# Revit family: ASL Door Suite 100mm
name_source: partatom
category: Doors
revit_build: Autodesk Revit 2018 (Build: 20170223_1515(x64)
units: mm (PartAtom-declared; Revit-internal decimal feet)

## family parameters
Always vertical = Yes
Cut with Voids When Loaded = No
OmniClass Number = 23.25.20.14.11.11.17
OmniClass Title = Infill Panels
Room Calculation Point = No
Shared = No

## types (5) — shared parameters
Analytic Construction = <None>
Frame Thickness = 44 mm  [stored 0.144357 ft]
Frame Width = 100 mm  [stored 0.328084 ft]
Glass Material = <By Category>
Manufacturer = Aluminate Solutions Limited
Material = <By Category>
Model = ASL Door Suite 100mm
Type Comments = ASL Door Suite 100mm

## per-type parameters (varying)
| type | Head Depth | Kickplate High | URL |
| 100mm Frame | 100 mm  [stored 0.328084 ft] | 100 mm  [stored 0.328084 ft] | http://www.productspec.net |
| 100mm Frame_150mm Kickplate | 100 mm  [stored 0.328084 ft] | 150 mm | http://www.productspec.net |
| 100mm Frame_75mm Kickplate | 100 mm  [stored 0.328084 ft] | 75 mm | www.aluminate.nz |
| 100mm Frame_75mm Head_75mm Kickplate | 75 mm | 75 mm | http://www.productspec.net |
| 100mm Frame_75mm Head_150mm Kickplate | 75 mm | 150 mm | http://www.productspec.net |

note: [stored X ft] marks values corroborated as IEEE doubles in the binary element streams (Revit-internal decimal feet)

## geometry (parser evidence)
native form markers: Sweep x2
no freeform markers — native parametric forms only
